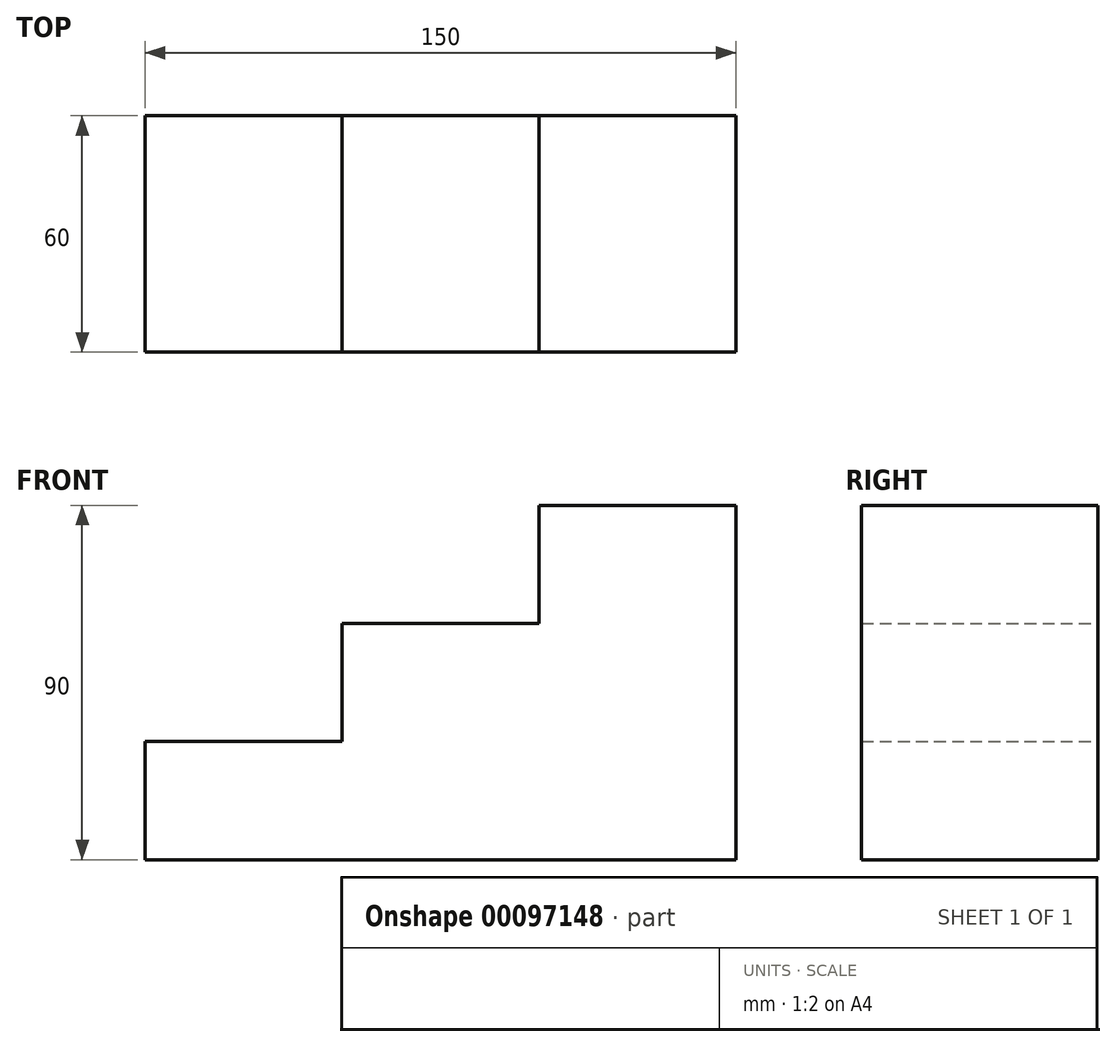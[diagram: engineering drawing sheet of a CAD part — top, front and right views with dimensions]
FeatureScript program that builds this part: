
annotation { "Feature Type Name" : "Feature", "Feature Type Description" : "" }
export const myFeature = defineFeature(function(context is Context, id is Id, definition is map)
    precondition{}
    {
        {
            var Q0;
            Q0=qCreatedBy(makeId("Front.planeOp"),FACE);
            var sketch = newSketch(context, id + "F0", { "sketchPlane" : qUnion([Q0])});
            skLineSegment(sketch, "E0", {"start": v(-150, 0) * mm, "end": v(-150, 30) * mm});
            skLineSegment(sketch, "E1", {"start": v(-150, 30) * mm, "end": v(-100, 30) * mm});
            skLineSegment(sketch, "E2", {"start": v(-100, 30) * mm, "end": v(-100, 60) * mm});
            skLineSegment(sketch, "E3", {"start": v(-100, 60) * mm, "end": v(-50, 60) * mm});
            skLineSegment(sketch, "E4", {"start": v(-50, 60) * mm, "end": v(-50, 90) * mm});
            skLineSegment(sketch, "E5", {"start": v(-50, 90) * mm, "end": v(0, 90) * mm});
            skLineSegment(sketch, "E6", {"start": v(0, 90) * mm, "end": v(0, 0) * mm});
            skLineSegment(sketch, "E7", {"start": v(0, 0) * mm, "end": v(-150, 0) * mm});
            skSolve(sketch);
        }
        {
            var Q0;
            Q0 = qSketchRegion(id + "F0", true);
            extrude(context, id + "F1", {"entities" : qUnion([Q0]), "depth" : 60 * mm});
        }
    });
